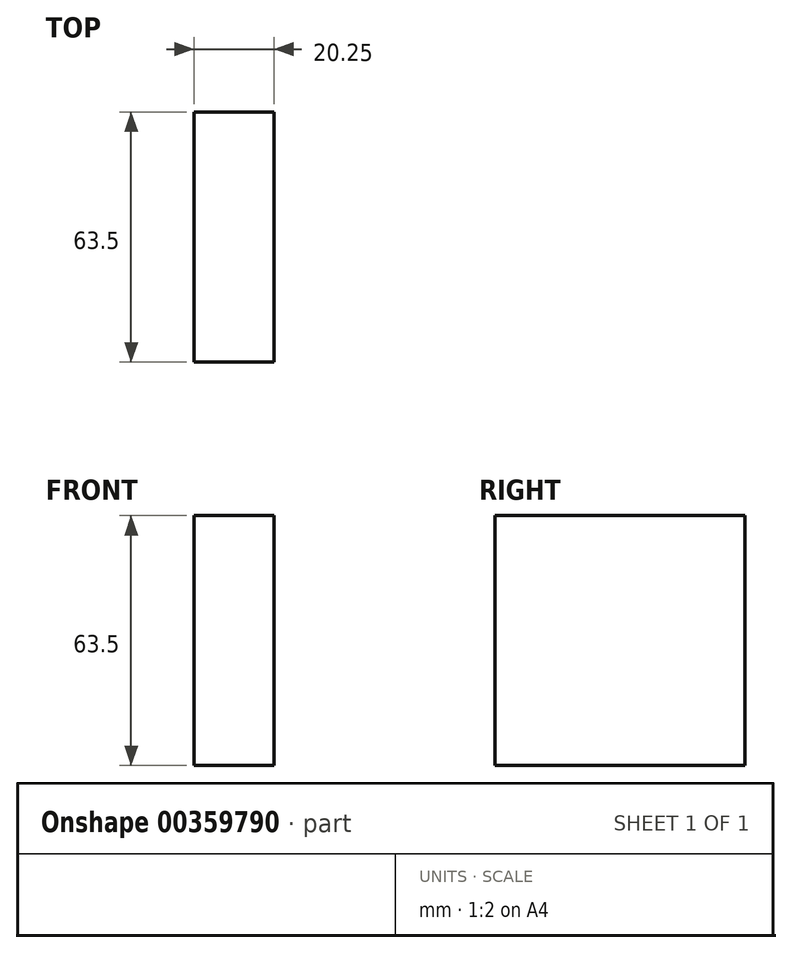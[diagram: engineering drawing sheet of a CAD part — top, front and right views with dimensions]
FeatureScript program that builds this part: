
annotation { "Feature Type Name" : "Feature", "Feature Type Description" : "" }
export const myFeature = defineFeature(function(context is Context, id is Id, definition is map)
    precondition{}
    {
        {
            var Q0;
            Q0=qCreatedBy(makeId("Front.planeOp"),FACE);
            var sketch = newSketch(context, id + "F0", { "sketchPlane" : qUnion([Q0])});
            skLineSegment(sketch, "E0.bottom", {"start": v(0, 0) * mm, "end": v(20.25, 0) * mm});
            skLineSegment(sketch, "E0.top", {"start": v(0, -63.5) * mm, "end": v(20.25, -63.5) * mm});
            skLineSegment(sketch, "E0.left", {"start": v(0, 0) * mm, "end": v(0, -63.5) * mm});
            skLineSegment(sketch, "E0.right", {"start": v(20.25, 0) * mm, "end": v(20.25, -63.5) * mm});
            skSolve(sketch);
        }
        {
            var Q0;
            Q0=makeQuery(id+"F0.imprint","IMPRINT",FACE,{"disambiguationData":[TD([[makeQuery(id+"F0.imprint","IMPRINT",EDGE,{"derivedFrom":sQuery(id+"F0.wireOp",EDGE,"E0.bottom")}),-1.0]])]});
            extrude(context, id + "F1", {"entities" : qUnion([Q0]), "depth" : 63.5 * mm});
        }
    });
